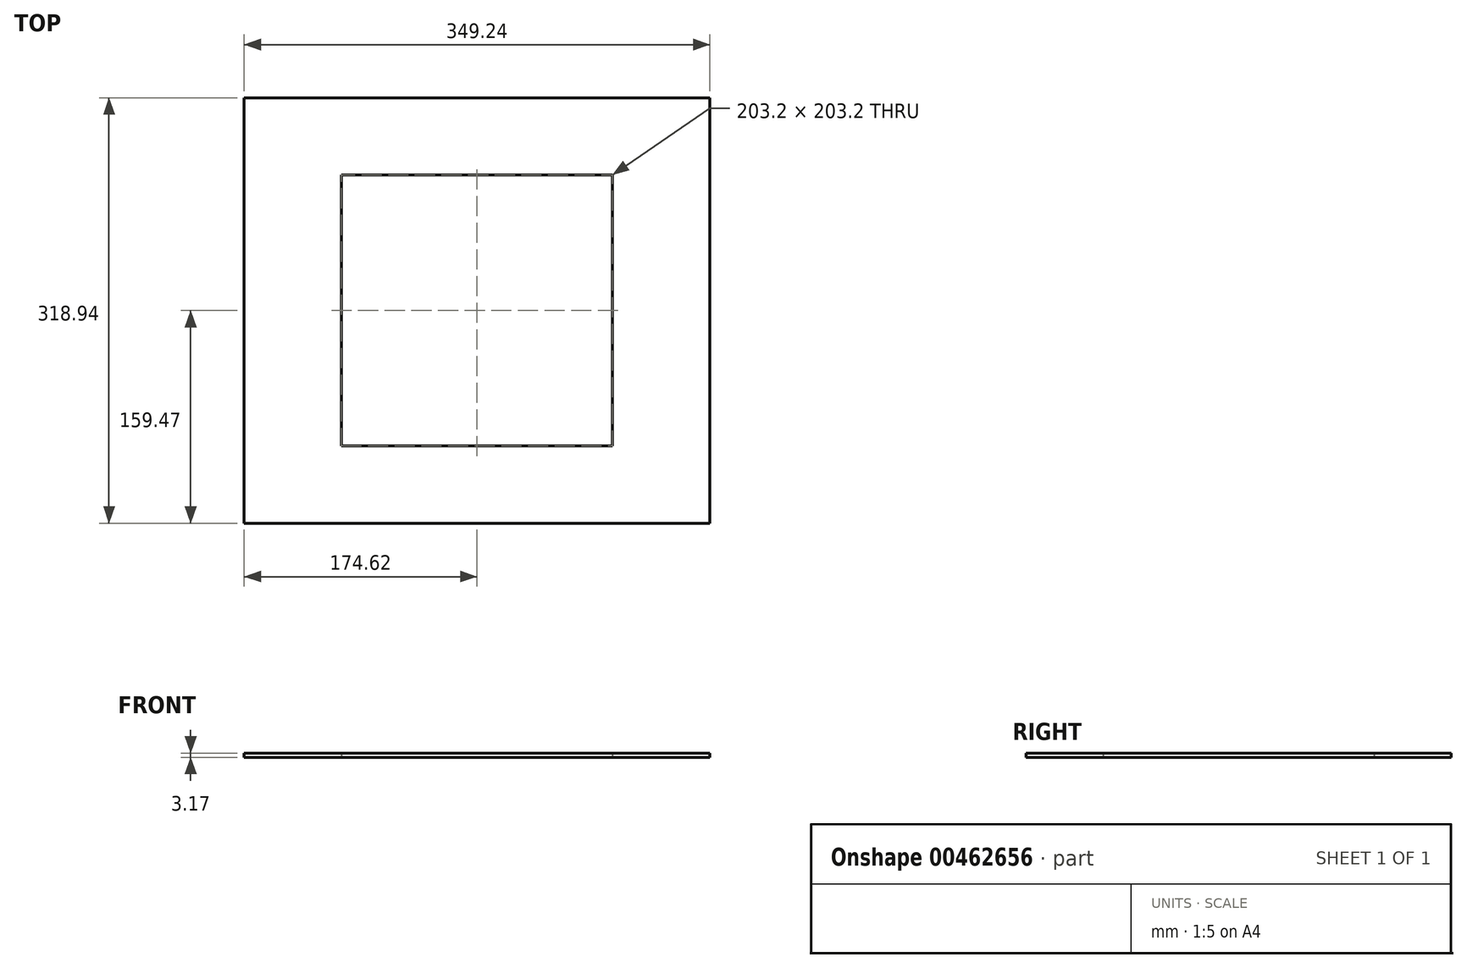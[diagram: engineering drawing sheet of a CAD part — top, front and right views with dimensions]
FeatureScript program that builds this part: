
annotation { "Feature Type Name" : "Feature", "Feature Type Description" : "" }
export const myFeature = defineFeature(function(context is Context, id is Id, definition is map)
    precondition{}
    {
        {
            var Q0;
            Q0=qCreatedBy(makeId("Top.planeOp"),FACE);
            var sketch = newSketch(context, id + "F0", { "sketchPlane" : qUnion([Q0])});
            skLineSegment(sketch, "E0.bottom", {"start": v(174.62, 159.47) * mm, "end": v(-174.62, 159.47) * mm});
            skLineSegment(sketch, "E0.top", {"start": v(174.62, -159.47) * mm, "end": v(-174.62, -159.47) * mm});
            skLineSegment(sketch, "E0.left", {"start": v(174.63, 159.47) * mm, "end": v(174.63, -159.47) * mm});
            skLineSegment(sketch, "E0.right", {"start": v(-174.63, 159.47) * mm, "end": v(-174.63, -159.47) * mm});
            skPoint(sketch, "E0.middle", {"position": v(0, 0) * mm});
            skLineSegment(sketch, "E1.bottom", {"start": v(101.6, 101.6) * mm, "end": v(-101.6, 101.6) * mm});
            skLineSegment(sketch, "E1.top", {"start": v(101.6, -101.6) * mm, "end": v(-101.6, -101.6) * mm});
            skLineSegment(sketch, "E1.left", {"start": v(101.6, 101.6) * mm, "end": v(101.6, -101.6) * mm});
            skLineSegment(sketch, "E1.right", {"start": v(-101.6, 101.6) * mm, "end": v(-101.6, -101.6) * mm});
            skSolve(sketch);
        }
        {
            var Q0;
            Q0=makeQuery(id+"F0.imprint","IMPRINT",FACE,{"disambiguationData":[TD([[makeQuery(id+"F0.imprint","IMPRINT",EDGE,{"derivedFrom":sQuery(id+"F0.wireOp",EDGE,"E0.bottom")}),1.0]])]});
            extrude(context, id + "F1", {"entities" : qUnion([Q0]), "depth" : 3.17 * mm});
        }
    });
